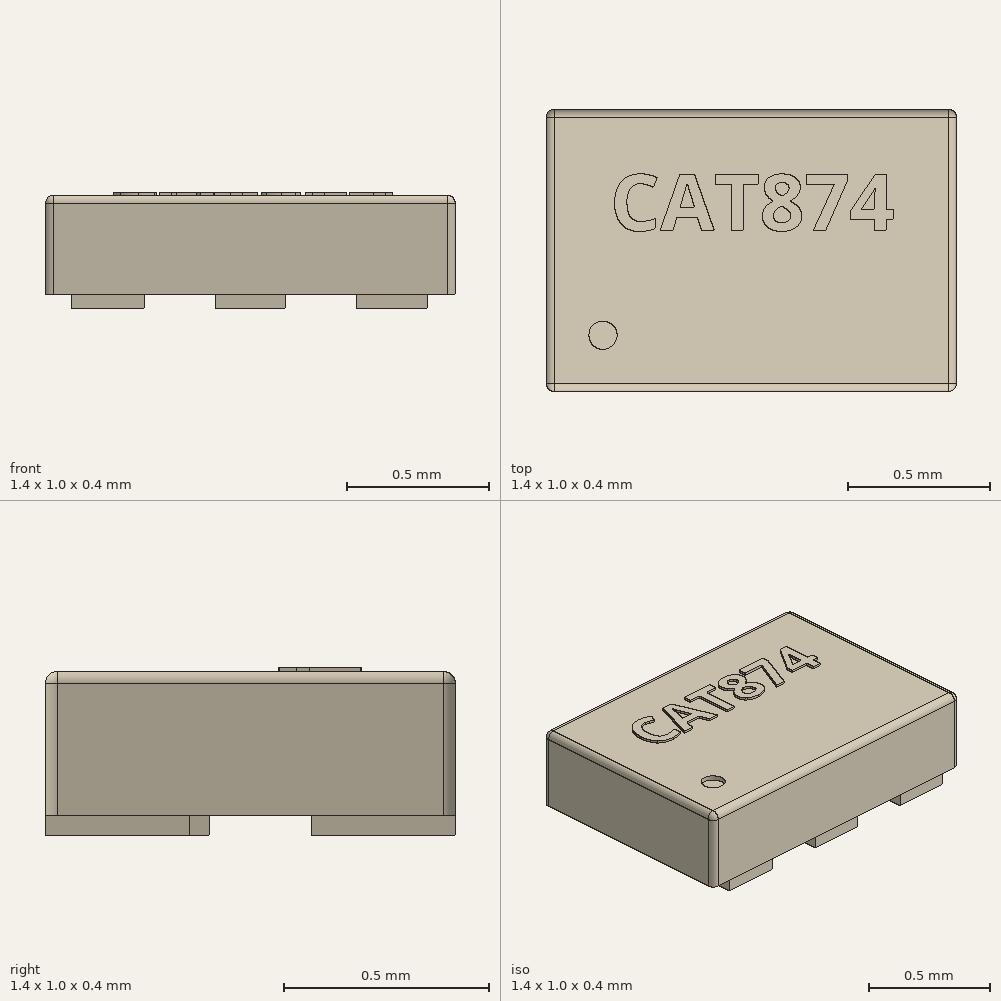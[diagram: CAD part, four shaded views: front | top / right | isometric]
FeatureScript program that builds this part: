
annotation { "Feature Type Name" : "Feature", "Feature Type Description" : "" }
export const myFeature = defineFeature(function(context is Context, id is Id, definition is map)
    precondition{}
    {
        {
            var Q0;
            Q0=qCreatedBy(makeId("Top.planeOp"),FACE);
            var sketch = newSketch(context, id + "F0", { "sketchPlane" : qUnion([Q0])});
            skLineSegment(sketch, "E0.bottom", {"start": v(-0.72, 0.5) * mm, "end": v(0.72, 0.5) * mm});
            skLineSegment(sketch, "E0.top", {"start": v(-0.73, -0.5) * mm, "end": v(0.72, -0.5) * mm});
            skLineSegment(sketch, "E0.left", {"start": v(-0.72, 0.5) * mm, "end": v(-0.73, -0.5) * mm});
            skLineSegment(sketch, "E0.right", {"start": v(0.73, 0.5) * mm, "end": v(0.72, -0.5) * mm});
            skPoint(sketch, "E0.middle", {"position": v(0, 0) * mm});
            skSolve(sketch);
        }
        {
            var Q0;
            Q0 = qSketchRegion(id + "F0", true);
            extrude(context, id + "F1", {"entities" : qUnion([Q0]), "depth" : 0.35 * mm});
        }
        {
            var Q0;
            Q0=makeQuery(id+"F1.opExtrude","CAP_FACE",FACE,{"disambiguationData":[OSD([sQuery(id+"F0.wireOp",EDGE,"E0.bottom"),sQuery(id+"F0.wireOp",EDGE,"E0.top"),sQuery(id+"F0.wireOp",EDGE,"E0.left"),sQuery(id+"F0.wireOp",EDGE,"E0.right")])],"isStart":false});
            var sketch = newSketch(context, id + "F2", { "sketchPlane" : qUnion([Q0])});
            skCircle(sketch, "E1", {"center": v(-0.53, -0.3) * mm, "radius": 0.05 * mm});
            skSolve(sketch);
        }
        {
            var Q0;
            Q0 = qSketchRegion(id + "F2", true);
            extrude(context, id + "F3", {"entities" : qUnion([Q0]), "operationType" : NewBodyOperationType.REMOVE, "oppositeDirection" : true, "depth" : 0.02 * mm});
        }
        {
            var Q0;
            Q0=makeQuery(id+"F1.opExtrude","CAP_FACE",FACE,{"disambiguationData":[OSD([sQuery(id+"F0.wireOp",EDGE,"E0.bottom"),sQuery(id+"F0.wireOp",EDGE,"E0.top"),sQuery(id+"F0.wireOp",EDGE,"E0.left"),sQuery(id+"F0.wireOp",EDGE,"E0.right")])],"isStart":true});
            var sketch = newSketch(context, id + "F4", { "sketchPlane" : qUnion([Q0])});
            skLineSegment(sketch, "E2.bottom", {"start": v(-0.12, 0.5) * mm, "end": v(0.12, 0.5) * mm});
            skLineSegment(sketch, "E2.top", {"start": v(-0.12, -0.5) * mm, "end": v(0.12, -0.5) * mm});
            skLineSegment(sketch, "E2.left", {"start": v(-0.12, 0.5) * mm, "end": v(-0.12, 0.15) * mm});
            skLineSegment(sketch, "E2.right", {"start": v(0.12, 0.5) * mm, "end": v(0.12, 0.15) * mm});
            skPoint(sketch, "E2.middle", {"position": v(0, 0) * mm});
            skLineSegment(sketch, "E3.top", {"start": v(-0.12, 0.15) * mm, "end": v(0.12, 0.15) * mm});
            skLineSegment(sketch, "E4.bottom", {"start": v(0.12, -0.5) * mm, "end": v(-0.12, -0.5) * mm});
            skLineSegment(sketch, "E4.top", {"start": v(0.12, -0.15) * mm, "end": v(-0.12, -0.15) * mm});
            skLineSegment(sketch, "E4.left", {"start": v(0.12, -0.5) * mm, "end": v(0.12, -0.15) * mm});
            skLineSegment(sketch, "E4.right", {"start": v(-0.12, -0.5) * mm, "end": v(-0.12, -0.15) * mm});
            skLineSegment(sketch, "E5.trimOffspring", {"start": v(-0.12, -0.15) * mm, "end": v(-0.12, -0.5) * mm});
            skLineSegment(sketch, "E6.trimOffspring", {"start": v(0.12, -0.15) * mm, "end": v(0.12, -0.5) * mm});
            skLineSegment(sketch, "E7.bottom", {"start": v(0.38, 0.5) * mm, "end": v(0.62, 0.5) * mm});
            skLineSegment(sketch, "E7.top", {"start": v(0.38, -0.5) * mm, "end": v(0.62, -0.5) * mm});
            skLineSegment(sketch, "E7.left", {"start": v(0.38, 0.5) * mm, "end": v(0.38, 0.15) * mm});
            skLineSegment(sketch, "E7.right", {"start": v(0.62, 0.5) * mm, "end": v(0.62, 0.15) * mm});
            skPoint(sketch, "E7.middle", {"position": v(0.5, 0) * mm});
            skLineSegment(sketch, "E8.bottom", {"start": v(-0.38, 0.5) * mm, "end": v(-0.63, 0.5) * mm});
            skLineSegment(sketch, "E8.top", {"start": v(-0.37, 0.15) * mm, "end": v(-0.58, 0.15) * mm});
            skLineSegment(sketch, "E8.left", {"start": v(-0.38, 0.5) * mm, "end": v(-0.37, 0.15) * mm});
            skLineSegment(sketch, "E8.right", {"start": v(-0.63, 0.5) * mm, "end": v(-0.63, 0.2) * mm});
            skLineSegment(sketch, "E9.bottom", {"start": v(-0.37, -0.15) * mm, "end": v(-0.63, -0.15) * mm});
            skLineSegment(sketch, "E9.top", {"start": v(-0.37, -0.5) * mm, "end": v(-0.63, -0.5) * mm});
            skLineSegment(sketch, "E9.left", {"start": v(-0.37, -0.15) * mm, "end": v(-0.37, -0.5) * mm});
            skLineSegment(sketch, "E9.right", {"start": v(-0.63, -0.15) * mm, "end": v(-0.63, -0.5) * mm});
            skLineSegment(sketch, "E10", {"start": v(0.38, 0.15) * mm, "end": v(0.62, 0.15) * mm});
            skLineSegment(sketch, "E11", {"start": v(0.38, -0.15) * mm, "end": v(0.62, -0.15) * mm});
            skLineSegment(sketch, "E12.trimOffspring", {"start": v(0.62, -0.15) * mm, "end": v(0.62, -0.5) * mm});
            skLineSegment(sketch, "E13.trimOffspring", {"start": v(0.38, -0.15) * mm, "end": v(0.38, -0.5) * mm});
            skLineSegment(sketch, "E14", {"start": v(-0.63, 0.2) * mm, "end": v(-0.58, 0.15) * mm});
            skPoint(sketch, "E15.orphan", {"position": v(-0.63, 0.15) * mm});
            skLineSegment(sketch, "E16", {"start": v(-0.58, 0.15) * mm, "end": v(-0.53, 0.1) * mm});
            skLineSegment(sketch, "E17", {"start": v(-0.53, 0.1) * mm, "end": v(-0.37, 0.1) * mm});
            skLineSegment(sketch, "E18", {"start": v(-0.37, 0.1) * mm, "end": v(-0.37, 0.15) * mm});
            skSolve(sketch);
        }
        {
            var Q0;
            Q0 = qSketchRegion(id + "F4", true);
            extrude(context, id + "F5", {"entities" : qUnion([Q0]), "depth" : 0.05 * mm});
        }
        {
            var Q0;
            Q0=makeQuery(id+"F1.opExtrude","CAP_FACE",FACE,{"disambiguationData":[OSD([sQuery(id+"F0.wireOp",EDGE,"E0.bottom"),sQuery(id+"F0.wireOp",EDGE,"E0.top"),sQuery(id+"F0.wireOp",EDGE,"E0.left"),sQuery(id+"F0.wireOp",EDGE,"E0.right")])],"isStart":false});
            var sketch = newSketch(context, id + "F6", { "sketchPlane" : qUnion([Q0])});
            skText(sketch, "E19", { "text": "CAT874", "fontName": "OpenSans-Bold.ttf"});
            const initialGuessF6  = {"E19": [-0.0005, 7e-05, 1, 0, 0.0002]};
            skSetInitialGuess(sketch, initialGuessF6);
            skSolve(sketch);
        }
        {
            var Q0;
            Q0 = qSketchRegion(id + "F6", true);
            extrude(context, id + "F7", {"entities" : qUnion([Q0]), "depth" : 0.01 * mm});
        }
        {
            var Q0;
            Q0=makeQuery(id+"F1.opExtrude","CAP_EDGE",EDGE,{"disambiguationData":[OSD([sQuery(id+"F0.wireOp",EDGE,"E0.top")])],"isStart":false});
            var Q1;
            Q1=makeQuery(id+"F1.opExtrude","CAP_EDGE",EDGE,{"disambiguationData":[OSD([sQuery(id+"F0.wireOp",EDGE,"E0.right")])],"isStart":false});
            var Q2;
            Q2=makeQuery(id+"F1.opExtrude","CAP_EDGE",EDGE,{"disambiguationData":[OSD([sQuery(id+"F0.wireOp",EDGE,"E0.bottom")])],"isStart":false});
            var Q3;
            Q3=makeQuery(id+"F1.opExtrude","CAP_EDGE",EDGE,{"disambiguationData":[OSD([sQuery(id+"F0.wireOp",EDGE,"E0.left")])],"isStart":false});
            var Q4;
            Q4=makeQuery(id+"F1.opExtrude","SWEPT_EDGE",EDGE,{"disambiguationData":[OSD([sQuery(id+"F0.wireOp",EDGE,"E0.top"),sQuery(id+"F0.wireOp",EDGE,"E0.right")])]});
            var Q5;
            Q5=makeQuery(id+"F1.opExtrude","SWEPT_EDGE",EDGE,{"disambiguationData":[OSD([sQuery(id+"F0.wireOp",EDGE,"E0.bottom"),sQuery(id+"F0.wireOp",EDGE,"E0.right")])]});
            var Q6;
            Q6=makeQuery(id+"F1.opExtrude","SWEPT_EDGE",EDGE,{"disambiguationData":[OSD([sQuery(id+"F0.wireOp",EDGE,"E0.bottom"),sQuery(id+"F0.wireOp",EDGE,"E0.left")])]});
            var Q7;
            Q7=makeQuery(id+"F1.opExtrude","SWEPT_EDGE",EDGE,{"disambiguationData":[OSD([sQuery(id+"F0.wireOp",EDGE,"E0.top"),sQuery(id+"F0.wireOp",EDGE,"E0.left")])]});
            fillet(context, id + "F8", {"entities" : qUnion([Q0, Q1, Q2, Q3, Q4, Q5, Q6, Q7]), "radius" : 0.03 * mm, "tangentPropagation" : true, "allowEdgeOverflow" : false});
        }
    });
